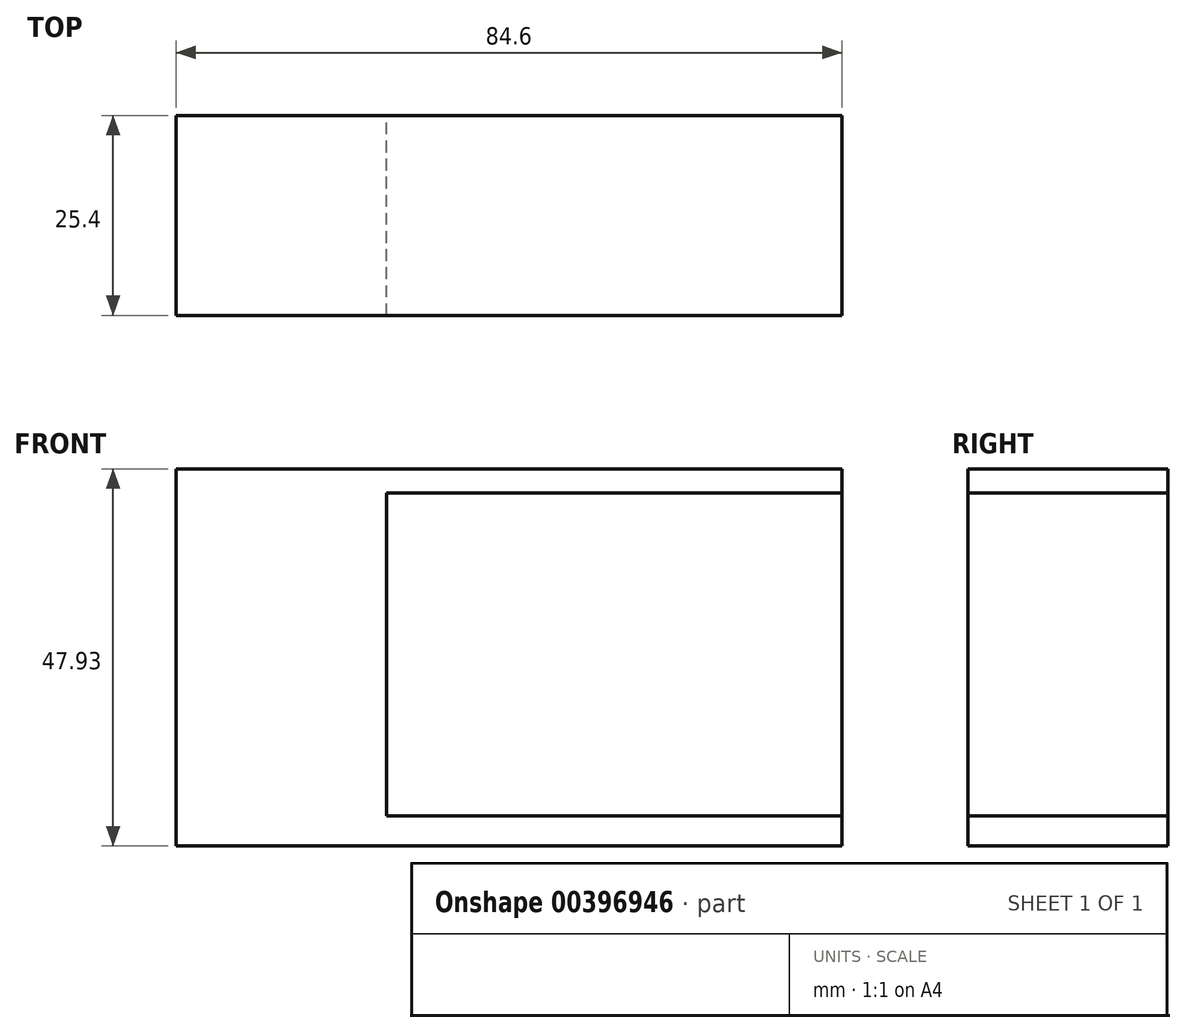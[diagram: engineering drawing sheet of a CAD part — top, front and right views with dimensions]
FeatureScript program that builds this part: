
annotation { "Feature Type Name" : "Feature", "Feature Type Description" : "" }
export const myFeature = defineFeature(function(context is Context, id is Id, definition is map)
    precondition{}
    {
        {
            var Q0;
            Q0=qCreatedBy(makeId("Front.planeOp"),FACE);
            var sketch = newSketch(context, id + "F0", { "sketchPlane" : qUnion([Q0])});
            skLineSegment(sketch, "E0.bottom", {"start": v(0, 0) * mm, "end": v(-59.2, 0) * mm});
            skLineSegment(sketch, "E0.top", {"start": v(0, 47.93) * mm, "end": v(-59.2, 47.93) * mm});
            skLineSegment(sketch, "E0.left", {"start": v(0, 0) * mm, "end": v(0, 47.93) * mm});
            skLineSegment(sketch, "E0.right", {"start": v(-59.2, 0) * mm, "end": v(-59.2, 47.93) * mm});
            skSolve(sketch);
        }
        {
            var Q0;
            Q0=makeQuery(id+"F0.imprint","IMPRINT",FACE,{"disambiguationData":[TD([[makeQuery(id+"F0.imprint","IMPRINT",EDGE,{"derivedFrom":sQuery(id+"F0.wireOp",EDGE,"E0.bottom")}),-1.0]])]});
            var sketch = newSketch(context, id + "F1", { "sketchPlane" : qUnion([Q0])});
            skLineSegment(sketch, "E1.bottom", {"start": v(-57.86, 44.87) * mm, "end": v(0, 44.87) * mm});
            skLineSegment(sketch, "E1.top", {"start": v(-57.86, 3.82) * mm, "end": v(0, 3.82) * mm});
            skLineSegment(sketch, "E1.left", {"start": v(-57.86, 44.87) * mm, "end": v(-57.86, 3.82) * mm});
            skLineSegment(sketch, "E1.right", {"start": v(0, 44.87) * mm, "end": v(0, 3.82) * mm});
            skSolve(sketch);
        }
        {
            var Q0;
            Q0=makeQuery(id+"F1.imprint","IMPRINT",FACE,{"disambiguationData":[TD([[makeQuery(id+"F1.imprint","IMPRINT",EDGE,{"derivedFrom":sQuery(id+"F1.wireOp",EDGE,"E1.bottom")}),-1.0]])]});
            var Q1;
            Q1=makeQuery(id+"F0.imprint","IMPRINT",FACE,{"disambiguationData":[TD([[makeQuery(id+"F0.imprint","IMPRINT",EDGE,{"derivedFrom":sQuery(id+"F0.wireOp",EDGE,"E0.bottom")}),-1.0]])]});
            extrude(context, id + "F2", {"entities" : qUnion([Q0, Q1]), "depth" : 25.4 * mm});
        }
        {
            var Q0;
            Q0=makeQuery(id+"F2.opExtrude","SWEPT_FACE",FACE,{"disambiguationData":[OSD([sQuery(id+"F0.wireOp",EDGE,"E0.right")])]});
            extrude(context, id + "F3", {"entities" : qUnion([Q0]), "operationType" : NewBodyOperationType.ADD, "depth" : 25.4 * mm});
        }
    });
